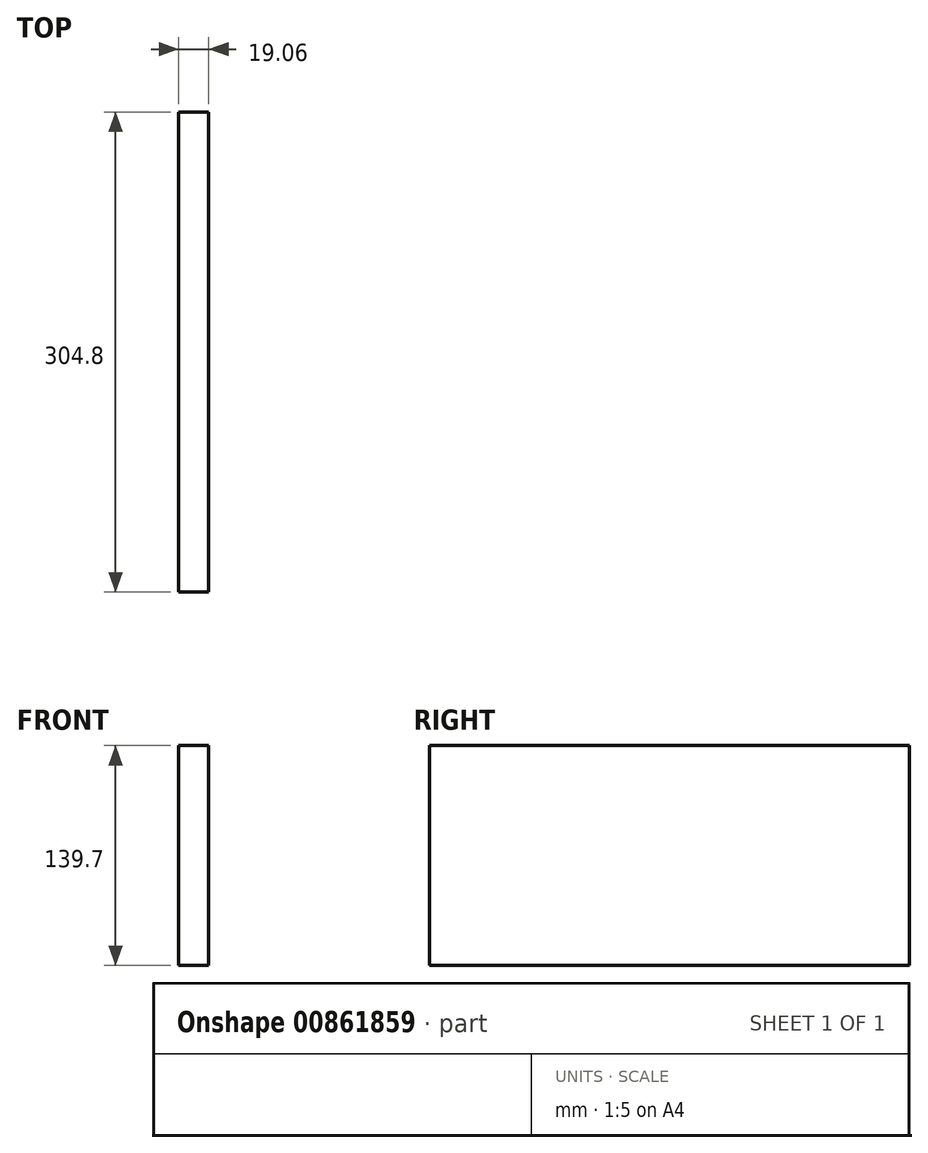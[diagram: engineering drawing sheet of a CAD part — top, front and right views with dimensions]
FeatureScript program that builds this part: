
annotation { "Feature Type Name" : "Feature", "Feature Type Description" : "" }
export const myFeature = defineFeature(function(context is Context, id is Id, definition is map)
    precondition{}
    {
        {
            var Q0;
            Q0=qCreatedBy(makeId("Front.planeOp"),FACE);
            var sketch = newSketch(context, id + "F0", { "sketchPlane" : qUnion([Q0])});
            skLineSegment(sketch, "E0.bottom", {"start": v(9.52, 69.85) * mm, "end": v(-9.53, 69.85) * mm});
            skLineSegment(sketch, "E0.top", {"start": v(9.52, -69.85) * mm, "end": v(-9.53, -69.85) * mm});
            skLineSegment(sketch, "E0.left", {"start": v(9.52, 69.85) * mm, "end": v(9.52, -69.85) * mm});
            skLineSegment(sketch, "E0.right", {"start": v(-9.53, 69.85) * mm, "end": v(-9.53, -69.85) * mm});
            skPoint(sketch, "E0.middle", {"position": v(0, 0) * mm});
            skSolve(sketch);
        }
        {
            var Q0;
            Q0=makeQuery(id+"F0.imprint","IMPRINT",FACE,{"disambiguationData":[TD([[makeQuery(id+"F0.imprint","IMPRINT",EDGE,{"derivedFrom":sQuery(id+"F0.wireOp",EDGE,"E0.bottom")}),1.0]])]});
            extrude(context, id + "F1", {"entities" : qUnion([Q0]), "depth" : 304.8 * mm, "offsetDistance" : 25.4 * mm});
        }
    });
